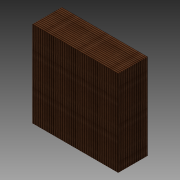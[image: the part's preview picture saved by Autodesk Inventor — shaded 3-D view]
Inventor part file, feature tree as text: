
AUTODESK INVENTOR PART (.ipt)
format: ipt  version: 2015 (Build 190159000, 159)  size: 107,008 bytes
history: native  units: mm
features: extrude x2, sketch x2
ambient origin geometry x8: Origin, YZ Plane, XZ Plane, XY Plane, X Axis, Y Axis, Z Axis, Center Point
bodies: Solide1 (feature_tree)
feature tree (4):
  extrude  "Extrusion1"  Depth=350.0mm
  extrude  "Extrusion2"  Depth=350.0mm
  sketch  "Esquisse1"
  sketch  "Esquisse2"
